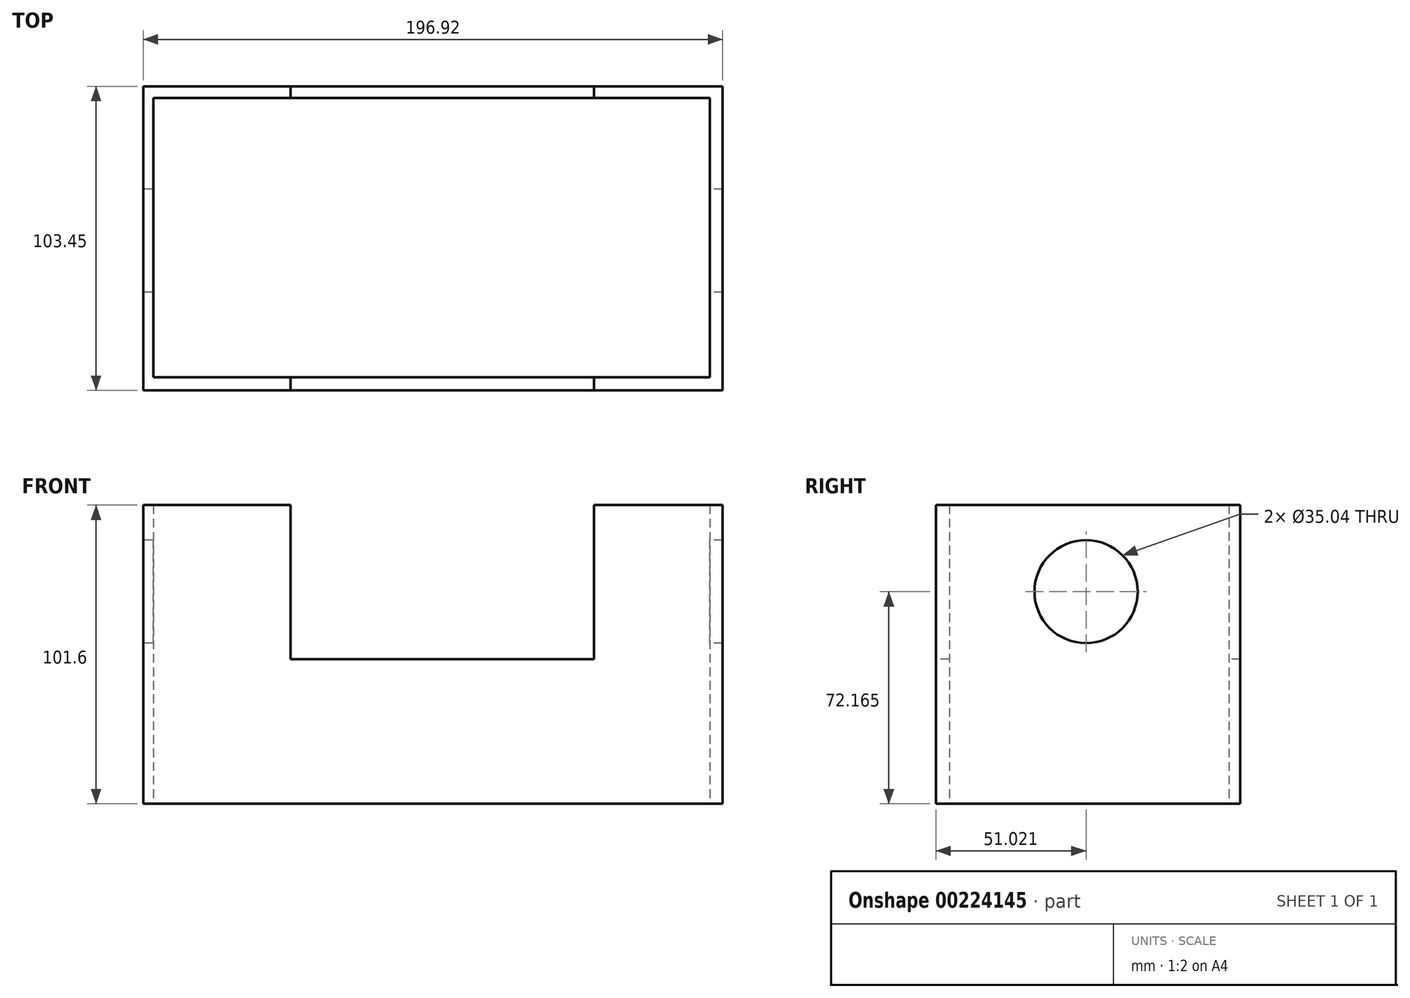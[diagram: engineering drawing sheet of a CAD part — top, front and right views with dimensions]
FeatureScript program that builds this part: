
annotation { "Feature Type Name" : "Feature", "Feature Type Description" : "" }
export const myFeature = defineFeature(function(context is Context, id is Id, definition is map)
    precondition{}
    {
        {
            var Q0;
            Q0=qCreatedBy(makeId("Top.planeOp"),FACE);
            var sketch = newSketch(context, id + "F0", { "sketchPlane" : qUnion([Q0])});
            skLineSegment(sketch, "E0.bottom", {"start": v(-98.31, 46.43) * mm, "end": v(98.61, 46.43) * mm});
            skLineSegment(sketch, "E0.top", {"start": v(-98.31, -57.02) * mm, "end": v(98.61, -57.02) * mm});
            skLineSegment(sketch, "E0.left", {"start": v(-98.31, 46.43) * mm, "end": v(-98.31, -57.02) * mm});
            skLineSegment(sketch, "E0.right", {"start": v(98.61, 46.43) * mm, "end": v(98.61, -57.02) * mm});
            skSolve(sketch);
        }
        {
            var Q0;
            Q0 = qSketchRegion(id + "F0", true);
            extrude(context, id + "F1", {"entities" : qUnion([Q0]), "depth" : 101.6 * mm});
        }
        {
            var Q0;
            Q0=makeQuery(id+"F1.opExtrude","SWEPT_FACE",FACE,{"disambiguationData":[OSD([sQuery(id+"F0.wireOp",EDGE,"E0.top")])]});
            var sketch = newSketch(context, id + "F2", { "sketchPlane" : qUnion([Q0])});
            skLineSegment(sketch, "E1.bottom", {"start": v(-48.2, 140.98) * mm, "end": v(54.85, 140.98) * mm});
            skLineSegment(sketch, "E1.top", {"start": v(-48.2, 49.23) * mm, "end": v(54.85, 49.23) * mm});
            skLineSegment(sketch, "E1.left", {"start": v(-48.2, 140.98) * mm, "end": v(-48.2, 49.23) * mm});
            skLineSegment(sketch, "E1.right", {"start": v(54.85, 140.98) * mm, "end": v(54.85, 49.23) * mm});
            skSolve(sketch);
        }
        {
            var Q0;
            Q0 = qSketchRegion(id + "F2", true);
            extrude(context, id + "F3", {"entities" : qUnion([Q0]), "operationType" : NewBodyOperationType.REMOVE, "endBound" : BoundingType.THROUGH_ALL, "oppositeDirection" : true, "depth" : 25.4 * mm});
        }
        {
            var Q0;
            Q0=makeQuery(id+"F1.opExtrude","SWEPT_FACE",FACE,{"disambiguationData":[OSD([sQuery(id+"F0.wireOp",EDGE,"E0.left")])]});
            var sketch = newSketch(context, id + "F4", { "sketchPlane" : qUnion([Q0])});
            skCircle(sketch, "E2", {"center": v(6, 72.17) * mm, "radius": 17.52 * mm});
            skSolve(sketch);
        }
        {
            var Q0;
            Q0 = qSketchRegion(id + "F4", true);
            extrude(context, id + "F5", {"entities" : qUnion([Q0]), "operationType" : NewBodyOperationType.REMOVE, "endBound" : BoundingType.THROUGH_ALL, "oppositeDirection" : true, "depth" : 25.4 * mm});
        }
        {
            var Q0;
            Q0=makeQuery(id+"F3.boolean.opBoolean","COPY",FACE,{"derivedFrom":makeQuery(id+"F3.opExtrude","SWEPT_FACE",FACE,{"disambiguationData":[OSD([sQuery(id+"F2.wireOp",EDGE,"E1.top")])]})});
            var sketch = newSketch(context, id + "F6", { "sketchPlane" : qUnion([Q0])});
            skLineSegment(sketch, "E3.bottom", {"start": v(-94.83, 42.5) * mm, "end": v(94.23, 42.5) * mm});
            skLineSegment(sketch, "E3.top", {"start": v(-94.83, -52.48) * mm, "end": v(94.23, -52.48) * mm});
            skLineSegment(sketch, "E3.left", {"start": v(-94.83, 42.5) * mm, "end": v(-94.83, -52.48) * mm});
            skLineSegment(sketch, "E3.right", {"start": v(94.23, 42.5) * mm, "end": v(94.23, -52.48) * mm});
            skSolve(sketch);
        }
        {
            var Q0;
            Q0 = qSketchRegion(id + "F6", true);
            extrude(context, id + "F7", {"entities" : qUnion([Q0]), "operationType" : NewBodyOperationType.REMOVE, "endBound" : BoundingType.THROUGH_ALL, "depth" : 25.4 * mm});
        }
        {
            var Q0;
            Q0=makeQuery(id+"F7.boolean.opBoolean","MERGE",FACE,{"derivedFrom":[makeQuery(id+"F3.boolean.opBoolean","COPY",FACE,{"derivedFrom":makeQuery(id+"F3.opExtrude","SWEPT_FACE",FACE,{"disambiguationData":[OSD([sQuery(id+"F2.wireOp",EDGE,"E1.top")])]})}),makeQuery(id+"F7.opExtrude","CAP_FACE",FACE,{"disambiguationData":[OSD([sQuery(id+"F6.wireOp",EDGE,"E3.bottom"),sQuery(id+"F6.wireOp",EDGE,"E3.top"),sQuery(id+"F6.wireOp",EDGE,"E3.left"),sQuery(id+"F6.wireOp",EDGE,"E3.right")])],"isStart":true})]});
            var sketch = newSketch(context, id + "F8", { "sketchPlane" : qUnion([Q0])});
            skLineSegment(sketch, "E4.bottom", {"start": v(-94.83, 42.5) * mm, "end": v(94.23, 42.5) * mm});
            skLineSegment(sketch, "E4.top", {"start": v(-94.83, -52.48) * mm, "end": v(94.23, -52.48) * mm});
            skLineSegment(sketch, "E4.left", {"start": v(-94.83, 42.5) * mm, "end": v(-94.83, -52.48) * mm});
            skLineSegment(sketch, "E4.right", {"start": v(94.23, 42.5) * mm, "end": v(94.23, -52.48) * mm});
            skSolve(sketch);
        }
        {
            var Q0;
            Q0 = qSketchRegion(id + "F8", true);
            extrude(context, id + "F9", {"entities" : qUnion([Q0]), "operationType" : NewBodyOperationType.REMOVE, "endBound" : BoundingType.THROUGH_ALL, "oppositeDirection" : true, "depth" : 25.4 * mm});
        }
    });
